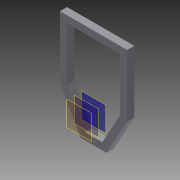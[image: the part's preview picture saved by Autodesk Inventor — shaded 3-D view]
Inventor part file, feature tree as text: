
AUTODESK INVENTOR PART (.ipt)
format: ipt  version: 2015 SP1 (Build 190203100, 203)  size: 139,264 bytes
history: native  units: in
note: dims shown in document units (in); Inventor stores cm internally (conversion verified against a paired STEP export)
features: plane x6, sketch x2, extrude x1
ambient origin geometry x8: Origin, YZ Plane, XZ Plane, XY Plane, X Axis, Y Axis, Z Axis, Center Point
bodies: Body1 (feature_tree)
feature tree (9):
  sketch  "Sketch1"  dims[d2=3.5in d3=2.25in]
  plane  "Work Plane2"
  plane  "Work Plane4"
  plane  "Work Plane3"
  plane  "Work Plane1"
  plane  "Work Plane6"
  sketch  "Sketch7"  dims[d4=11.0in d5=6.0in d8=3.0in d10=0.5in d11=0.4in d12=0.4in d13=0.4in d14=0.5in d15=0.4in d16=0.4in d17=0.4in d18=0.5in d19=0.5in d42=0.1in d96=4.5in d97=0.75in d98=1.0in d99=1.25in d100=1.0in d101=1.25in d102=0.5in d111=0.0in d120=1.0in d121=0.4in d126=2.4in d127=0.25in d128=0.02in d129=0.25in d130=0.0in d131=1.0378in d134=2.5in d135=1.2in d136=2.2017in d137=1.3288in]
  plane  "Work Plane5"
  extrude  "Extrusion14"  Depth=2.25in
